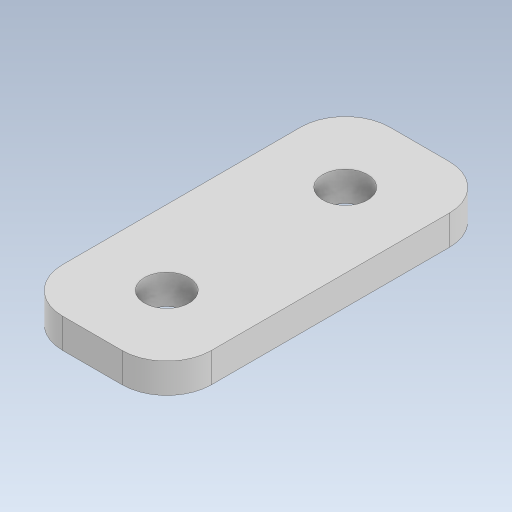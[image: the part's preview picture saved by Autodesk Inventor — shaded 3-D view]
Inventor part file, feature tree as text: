
AUTODESK INVENTOR PART (.ipt)
format: ipt  version: 2023.5 (Build 275446000, 446)  size: 107,520 bytes
history: native  units: in
note: dims shown in document units (in); Inventor stores cm internally (conversion verified against a paired STEP export)
features: extrude x1, sketch x1
ambient origin geometry x8: Origin, YZ Plane, XZ Plane, XY Plane, X Axis, Y Axis, Z Axis, Center Point
bodies: Solid1 (feature_tree)
feature tree (2):
  extrude  "Extrusion1"  Depth=0.2362in
  sketch  "Sketch1"  dims[d0=0.1181in d1=0.2362in d2=0.1969in d3=0.1969in d4=0.1181in d5=0.0787in d6=0.0in]
